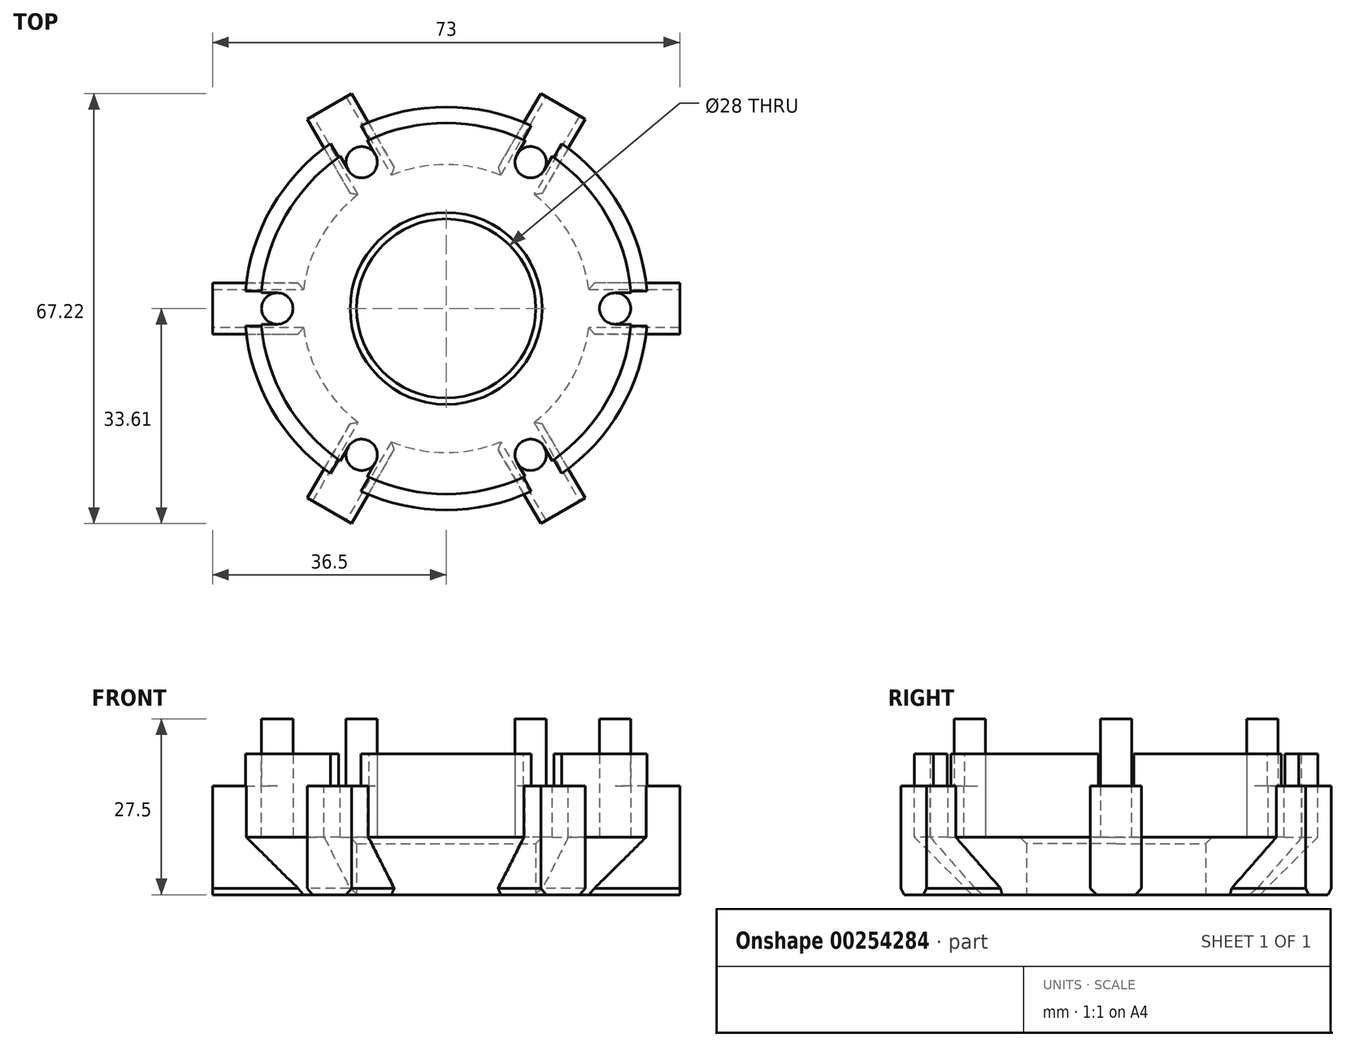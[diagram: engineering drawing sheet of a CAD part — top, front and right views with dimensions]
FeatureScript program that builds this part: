
annotation { "Feature Type Name" : "Feature", "Feature Type Description" : "" }
export const myFeature = defineFeature(function(context is Context, id is Id, definition is map)
    precondition{}
    {
        {
            var Q0;
            Q0=qCreatedBy(makeId("Top.planeOp"),FACE);
            var sketch = newSketch(context, id + "F0", { "sketchPlane" : qUnion([Q0])});
            skCircle(sketch, "E0", {"center": v(0, 0) * mm, "radius": 31.5 * mm});
            skSolve(sketch);
        }
        {
            var Q0;
            Q0 = qSketchRegion(id + "F0", true);
            extrude(context, id + "F1", {"entities" : qUnion([Q0]), "oppositeDirection" : true, "depth" : 22 * mm});
        }
        {
            var Q0;
            Q0=makeQuery(id+"F1.opExtrude","CAP_FACE",FACE,{"disambiguationData":[OSD([sQuery(id+"F0.wireOp",EDGE,"E0")])],"isStart":true});
            var sketch = newSketch(context, id + "F2", { "sketchPlane" : qUnion([Q0])});
            skCircle(sketch, "E1.0", {"center": v(0, 0) * mm, "radius": 29 * mm});
            skSolve(sketch);
        }
        {
            var Q0;
            Q0=makeQuery(id+"F1.opExtrude","CAP_FACE",FACE,{"disambiguationData":[OSD([sQuery(id+"F0.wireOp",EDGE,"E0")])],"isStart":false});
            var sketch = newSketch(context, id + "F3", { "sketchPlane" : qUnion([Q0])});
            skCircle(sketch, "E2", {"center": v(0, 0) * mm, "radius": 14 * mm});
            skSolve(sketch);
        }
        {
            var Q0;
            Q0 = qSketchRegion(id + "F3", true);
            extrude(context, id + "F4", {"entities" : qUnion([Q0]), "operationType" : NewBodyOperationType.REMOVE, "endBound" : BoundingType.THROUGH_ALL, "oppositeDirection" : true, "depth" : 25 * mm});
        }
        {
            var Q0;
            Q0=makeQuery(id+"F1.opExtrude","CAP_EDGE",EDGE,{"disambiguationData":[OSD([sQuery(id+"F0.wireOp",EDGE,"E0")])],"isStart":false});
            chamfer(context, id + "F5", {"entities" : qUnion([Q0]), "width" : 9 * mm, "tangentPropagation" : true});
        }
        {
            var Q0;
            Q0=makeQuery(id+"F1.opExtrude","CAP_FACE",FACE,{"disambiguationData":[OSD([sQuery(id+"F0.wireOp",EDGE,"E0")])],"isStart":false});
            var sketch = newSketch(context, id + "F6", { "sketchPlane" : qUnion([Q0])});
            skLineSegment(sketch, "E3.bottom", {"start": v(36.5, 4) * mm, "end": v(21.5, 4) * mm});
            skLineSegment(sketch, "E3.top", {"start": v(36.5, -4) * mm, "end": v(21.5, -4) * mm});
            skLineSegment(sketch, "E3.left", {"start": v(36.5, 4) * mm, "end": v(36.5, -4) * mm});
            skLineSegment(sketch, "E3.right", {"start": v(21.5, 4) * mm, "end": v(21.5, -4) * mm});
            skLineSegment(sketch, "E4.1.0", {"start": v(14.79, 33.6) * mm, "end": v(7.29, 20.62) * mm});
            skLineSegment(sketch, "E4.1.1", {"start": v(14.79, 33.6) * mm, "end": v(21.71, 29.6) * mm});
            skLineSegment(sketch, "E4.1.2", {"start": v(21.71, 29.6) * mm, "end": v(14.21, 16.62) * mm});
            skLineSegment(sketch, "E4.1.3", {"start": v(7.29, 20.62) * mm, "end": v(14.21, 16.62) * mm});
            skLineSegment(sketch, "E4.2.0", {"start": v(-21.71, 29.6) * mm, "end": v(-14.21, 16.62) * mm});
            skLineSegment(sketch, "E4.2.1", {"start": v(-21.71, 29.6) * mm, "end": v(-14.79, 33.6) * mm});
            skLineSegment(sketch, "E4.2.2", {"start": v(-14.79, 33.6) * mm, "end": v(-7.29, 20.62) * mm});
            skLineSegment(sketch, "E4.2.3", {"start": v(-14.21, 16.62) * mm, "end": v(-7.29, 20.62) * mm});
            skLineSegment(sketch, "E4.3.0", {"start": v(-36.5, -4) * mm, "end": v(-21.5, -4) * mm});
            skLineSegment(sketch, "E4.3.1", {"start": v(-36.5, -4) * mm, "end": v(-36.5, 4) * mm});
            skLineSegment(sketch, "E4.3.2", {"start": v(-36.5, 4) * mm, "end": v(-21.5, 4) * mm});
            skLineSegment(sketch, "E4.3.3", {"start": v(-21.5, -4) * mm, "end": v(-21.5, 4) * mm});
            skLineSegment(sketch, "E4.4.0", {"start": v(-14.79, -33.6) * mm, "end": v(-7.29, -20.62) * mm});
            skLineSegment(sketch, "E4.4.1", {"start": v(-14.79, -33.6) * mm, "end": v(-21.71, -29.6) * mm});
            skLineSegment(sketch, "E4.4.2", {"start": v(-21.71, -29.6) * mm, "end": v(-14.21, -16.62) * mm});
            skLineSegment(sketch, "E4.4.3", {"start": v(-7.29, -20.62) * mm, "end": v(-14.21, -16.62) * mm});
            skLineSegment(sketch, "E4.5.0", {"start": v(21.71, -29.6) * mm, "end": v(14.21, -16.62) * mm});
            skLineSegment(sketch, "E4.5.1", {"start": v(21.71, -29.6) * mm, "end": v(14.79, -33.6) * mm});
            skLineSegment(sketch, "E4.5.2", {"start": v(14.79, -33.6) * mm, "end": v(7.29, -20.62) * mm});
            skLineSegment(sketch, "E4.5.3", {"start": v(14.21, -16.62) * mm, "end": v(7.29, -20.62) * mm});
            skPoint(sketch, "E4.center", {"position": v(0, 0) * mm});
            skSolve(sketch);
        }
        {
            var Q0;
            Q0 = qSketchRegion(id + "F6", true);
            extrude(context, id + "F7", {"entities" : qUnion([Q0]), "operationType" : NewBodyOperationType.ADD, "oppositeDirection" : true, "depth" : 17 * mm});
        }
        {
            var Q0;
            Q0=makeQuery(id+"F2.imprint","IMPRINT",FACE,{"disambiguationData":[TD([[makeQuery(id+"F2.imprint","IMPRINT",EDGE,{"derivedFrom":sQuery(id+"F2.wireOp",EDGE,"E1.0")}),1.0]])]});
            extrude(context, id + "F8", {"entities" : qUnion([Q0]), "operationType" : NewBodyOperationType.REMOVE, "oppositeDirection" : true, "depth" : 13 * mm});
        }
        {
            var Q0;
            Q0=makeQuery(id+"F1.opExtrude","CAP_FACE",FACE,{"disambiguationData":[OSD([sQuery(id+"F0.wireOp",EDGE,"E0")])],"isStart":true});
            var sketch = newSketch(context, id + "F9", { "sketchPlane" : qUnion([Q0])});
            skLineSegment(sketch, "E5.bottom", {"start": v(36.1, 2.75) * mm, "end": v(24.5, 2.75) * mm});
            skLineSegment(sketch, "E5.top", {"start": v(36.1, -2.75) * mm, "end": v(24.5, -2.75) * mm});
            skLineSegment(sketch, "E5.left", {"start": v(36.1, 2.75) * mm, "end": v(36.1, -2.75) * mm});
            skLineSegment(sketch, "E5.right", {"start": v(24.5, 2.75) * mm, "end": v(24.5, -2.75) * mm});
            skLineSegment(sketch, "E6.1.0", {"start": v(15.67, 32.65) * mm, "end": v(9.87, 22.6) * mm});
            skLineSegment(sketch, "E6.1.1", {"start": v(15.67, 32.65) * mm, "end": v(20.44, 29.9) * mm});
            skLineSegment(sketch, "E6.1.2", {"start": v(20.44, 29.9) * mm, "end": v(14.63, 19.84) * mm});
            skLineSegment(sketch, "E6.1.3", {"start": v(9.87, 22.6) * mm, "end": v(14.63, 19.84) * mm});
            skLineSegment(sketch, "E6.2.0", {"start": v(-20.44, 29.9) * mm, "end": v(-14.63, 19.84) * mm});
            skLineSegment(sketch, "E6.2.1", {"start": v(-20.44, 29.9) * mm, "end": v(-15.67, 32.65) * mm});
            skLineSegment(sketch, "E6.2.2", {"start": v(-15.67, 32.65) * mm, "end": v(-9.87, 22.6) * mm});
            skLineSegment(sketch, "E6.2.3", {"start": v(-14.63, 19.84) * mm, "end": v(-9.87, 22.6) * mm});
            skLineSegment(sketch, "E6.3.0", {"start": v(-36.1, -2.75) * mm, "end": v(-24.5, -2.75) * mm});
            skLineSegment(sketch, "E6.3.1", {"start": v(-36.1, -2.75) * mm, "end": v(-36.1, 2.75) * mm});
            skLineSegment(sketch, "E6.3.2", {"start": v(-36.1, 2.75) * mm, "end": v(-24.5, 2.75) * mm});
            skLineSegment(sketch, "E6.3.3", {"start": v(-24.5, -2.75) * mm, "end": v(-24.5, 2.75) * mm});
            skLineSegment(sketch, "E6.4.0", {"start": v(-15.67, -32.65) * mm, "end": v(-9.87, -22.6) * mm});
            skLineSegment(sketch, "E6.4.1", {"start": v(-15.67, -32.65) * mm, "end": v(-20.44, -29.9) * mm});
            skLineSegment(sketch, "E6.4.2", {"start": v(-20.44, -29.9) * mm, "end": v(-14.63, -19.84) * mm});
            skLineSegment(sketch, "E6.4.3", {"start": v(-9.87, -22.6) * mm, "end": v(-14.63, -19.84) * mm});
            skLineSegment(sketch, "E6.5.0", {"start": v(20.44, -29.9) * mm, "end": v(14.63, -19.84) * mm});
            skLineSegment(sketch, "E6.5.1", {"start": v(20.44, -29.9) * mm, "end": v(15.67, -32.65) * mm});
            skLineSegment(sketch, "E6.5.2", {"start": v(15.67, -32.65) * mm, "end": v(9.87, -22.6) * mm});
            skLineSegment(sketch, "E6.5.3", {"start": v(14.63, -19.84) * mm, "end": v(9.87, -22.6) * mm});
            skPoint(sketch, "E6.center", {"position": v(0, 0) * mm});
            skSolve(sketch);
        }
        {
            var Q0;
            Q0 = qSketchRegion(id + "F9", true);
            extrude(context, id + "F10", {"entities" : qUnion([Q0]), "operationType" : NewBodyOperationType.REMOVE, "oppositeDirection" : true, "depth" : 5 * mm});
        }
        {
            var Q0;
            Q0=makeQuery(id+"F8.boolean.opBoolean","COPY",FACE,{"derivedFrom":makeQuery(id+"F8.opExtrude","CAP_FACE",FACE,{"disambiguationData":[OSD([sQuery(id+"F2.wireOp",EDGE,"E1.0")])],"isStart":false})});
            var sketch = newSketch(context, id + "F11", { "sketchPlane" : qUnion([Q0])});
            skCircle(sketch, "E7", {"center": v(-26.4, 0) * mm, "radius": 2.45 * mm});
            skCircle(sketch, "E8.1.0", {"center": v(-13.2, -22.86) * mm, "radius": 2.45 * mm});
            skCircle(sketch, "E8.2.0", {"center": v(13.2, -22.86) * mm, "radius": 2.45 * mm});
            skCircle(sketch, "E8.3.0", {"center": v(26.4, 0) * mm, "radius": 2.45 * mm});
            skCircle(sketch, "E8.4.0", {"center": v(13.2, 22.86) * mm, "radius": 2.45 * mm});
            skCircle(sketch, "E8.5.0", {"center": v(-13.2, 22.86) * mm, "radius": 2.45 * mm});
            skPoint(sketch, "E8.center", {"position": v(0, 0) * mm});
            skSolve(sketch);
        }
        {
            var Q0;
            Q0 = qSketchRegion(id + "F11", true);
            extrude(context, id + "F12", {"entities" : qUnion([Q0]), "operationType" : NewBodyOperationType.ADD, "depth" : 18.5 * mm});
        }
        {
            var Q0;
            Q0=makeQuery(id+"F8.boolean.opBoolean","COPY",FACE,{"derivedFrom":makeQuery(id+"F8.opExtrude","CAP_FACE",FACE,{"disambiguationData":[OSD([sQuery(id+"F2.wireOp",EDGE,"E1.0")])],"isStart":false})});
            var sketch = newSketch(context, id + "F13", { "sketchPlane" : qUnion([Q0])});
            skLineSegment(sketch, "E9.bottom", {"start": v(-29.72, -2.45) * mm, "end": v(-26.4, -2.45) * mm});
            skLineSegment(sketch, "E9.top", {"start": v(-29.72, 2.45) * mm, "end": v(-26.4, 2.45) * mm});
            skLineSegment(sketch, "E9.left", {"start": v(-29.72, -2.45) * mm, "end": v(-29.72, 2.45) * mm});
            skLineSegment(sketch, "E9.right", {"start": v(-26.4, -2.45) * mm, "end": v(-26.4, 2.45) * mm});
            skLineSegment(sketch, "E10.1.0", {"start": v(-12.74, -26.96) * mm, "end": v(-16.98, -24.51) * mm});
            skLineSegment(sketch, "E10.1.1", {"start": v(-16.98, -24.51) * mm, "end": v(-15.32, -21.64) * mm});
            skLineSegment(sketch, "E10.1.2", {"start": v(-11.08, -24.09) * mm, "end": v(-15.32, -21.64) * mm});
            skLineSegment(sketch, "E10.1.3", {"start": v(-12.74, -26.96) * mm, "end": v(-11.08, -24.09) * mm});
            skLineSegment(sketch, "E10.2.0", {"start": v(16.98, -24.51) * mm, "end": v(12.74, -26.96) * mm});
            skLineSegment(sketch, "E10.2.1", {"start": v(12.74, -26.96) * mm, "end": v(11.08, -24.09) * mm});
            skLineSegment(sketch, "E10.2.2", {"start": v(15.32, -21.64) * mm, "end": v(11.08, -24.09) * mm});
            skLineSegment(sketch, "E10.2.3", {"start": v(16.98, -24.51) * mm, "end": v(15.32, -21.64) * mm});
            skLineSegment(sketch, "E10.3.0", {"start": v(29.72, 2.45) * mm, "end": v(29.72, -2.45) * mm});
            skLineSegment(sketch, "E10.3.1", {"start": v(29.72, -2.45) * mm, "end": v(26.4, -2.45) * mm});
            skLineSegment(sketch, "E10.3.2", {"start": v(26.4, 2.45) * mm, "end": v(26.4, -2.45) * mm});
            skLineSegment(sketch, "E10.3.3", {"start": v(29.72, 2.45) * mm, "end": v(26.4, 2.45) * mm});
            skLineSegment(sketch, "E10.4.0", {"start": v(12.74, 26.96) * mm, "end": v(16.98, 24.51) * mm});
            skLineSegment(sketch, "E10.4.1", {"start": v(16.98, 24.51) * mm, "end": v(15.32, 21.64) * mm});
            skLineSegment(sketch, "E10.4.2", {"start": v(11.08, 24.09) * mm, "end": v(15.32, 21.64) * mm});
            skLineSegment(sketch, "E10.4.3", {"start": v(12.74, 26.96) * mm, "end": v(11.08, 24.09) * mm});
            skLineSegment(sketch, "E10.5.0", {"start": v(-16.98, 24.51) * mm, "end": v(-12.74, 26.96) * mm});
            skLineSegment(sketch, "E10.5.1", {"start": v(-12.74, 26.96) * mm, "end": v(-11.08, 24.09) * mm});
            skLineSegment(sketch, "E10.5.2", {"start": v(-15.32, 21.64) * mm, "end": v(-11.08, 24.09) * mm});
            skLineSegment(sketch, "E10.5.3", {"start": v(-16.98, 24.51) * mm, "end": v(-15.32, 21.64) * mm});
            skPoint(sketch, "E10.center", {"position": v(0, 0) * mm});
            skSolve(sketch);
        }
        {
            var Q0;
            Q0 = qSketchRegion(id + "F13", true);
            extrude(context, id + "F14", {"entities" : qUnion([Q0]), "operationType" : NewBodyOperationType.ADD, "depth" : 8 * mm});
        }
        {
            var Q0;
            Q0=makeQuery(id+"F4.boolean.opBoolean","COPY",EDGE,{"derivedFrom":makeQuery(id+"F4.opExtrude","CAP_EDGE",EDGE,{"disambiguationData":[OSD([sQuery(id+"F3.wireOp",EDGE,"E2")])],"isStart":true})});
            var Q1;
            Q1=makeQuery(id+"F8.boolean.opBoolean","INTERSECT",EDGE,{"derivedFrom":[makeQuery(id+"F4.boolean.opBoolean","COPY",FACE,{"derivedFrom":makeQuery(id+"F4.opExtrude","SWEPT_FACE",FACE,{"disambiguationData":[OSD([sQuery(id+"F3.wireOp",EDGE,"E2")])]})}),makeQuery(id+"F8.opExtrude","CAP_FACE",FACE,{"disambiguationData":[OSD([sQuery(id+"F2.wireOp",EDGE,"E1.0")])],"isStart":false})]});
            var Q2;
            Q2=makeQuery(id+"F7.opExtrude","CAP_EDGE",EDGE,{"disambiguationData":[OSD([sQuery(id+"F6.wireOp",EDGE,"E4.2.0")])],"isStart":true});
            var Q3;
            Q3=makeQuery(id+"F7.opExtrude","CAP_EDGE",EDGE,{"disambiguationData":[OSD([sQuery(id+"F6.wireOp",EDGE,"E4.2.2")])],"isStart":true});
            var Q4;
            Q4=makeQuery(id+"F7.opExtrude","CAP_EDGE",EDGE,{"disambiguationData":[OSD([sQuery(id+"F6.wireOp",EDGE,"E4.1.0")])],"isStart":true});
            var Q5;
            Q5=makeQuery(id+"F7.opExtrude","CAP_EDGE",EDGE,{"disambiguationData":[OSD([sQuery(id+"F6.wireOp",EDGE,"E4.1.2")])],"isStart":true});
            var Q6;
            Q6=makeQuery(id+"F7.opExtrude","CAP_EDGE",EDGE,{"disambiguationData":[OSD([sQuery(id+"F6.wireOp",EDGE,"E3.bottom")])],"isStart":true});
            var Q7;
            Q7=makeQuery(id+"F7.opExtrude","CAP_EDGE",EDGE,{"disambiguationData":[OSD([sQuery(id+"F6.wireOp",EDGE,"E3.top")])],"isStart":true});
            var Q8;
            Q8=makeQuery(id+"F7.opExtrude","CAP_EDGE",EDGE,{"disambiguationData":[OSD([sQuery(id+"F6.wireOp",EDGE,"E4.5.0")])],"isStart":true});
            var Q9;
            Q9=makeQuery(id+"F7.opExtrude","CAP_EDGE",EDGE,{"disambiguationData":[OSD([sQuery(id+"F6.wireOp",EDGE,"E4.5.2")])],"isStart":true});
            var Q10;
            Q10=makeQuery(id+"F7.opExtrude","CAP_EDGE",EDGE,{"disambiguationData":[OSD([sQuery(id+"F6.wireOp",EDGE,"E4.4.0")])],"isStart":true});
            var Q11;
            Q11=makeQuery(id+"F7.opExtrude","CAP_EDGE",EDGE,{"disambiguationData":[OSD([sQuery(id+"F6.wireOp",EDGE,"E4.4.2")])],"isStart":true});
            var Q12;
            Q12=makeQuery(id+"F7.opExtrude","CAP_EDGE",EDGE,{"disambiguationData":[OSD([sQuery(id+"F6.wireOp",EDGE,"E4.3.0")])],"isStart":true});
            var Q13;
            Q13=makeQuery(id+"F7.opExtrude","CAP_EDGE",EDGE,{"disambiguationData":[OSD([sQuery(id+"F6.wireOp",EDGE,"E4.3.2")])],"isStart":true});
            chamfer(context, id + "F15", {"entities" : qUnion([Q0, Q1, Q2, Q3, Q4, Q5, Q6, Q7, Q8, Q9, Q10, Q11, Q12, Q13]), "width" : 1 * mm, "tangentPropagation" : true});
        }
    });
